SOLIDWORKS PART (.sldprt)
format: sldprt  version: not decoded by parser v0  size: 262,656 bytes
history: native  units: mm
features: sketch x7, cut_extrude x4, material x1, extrude x1, plane x1, mirror x1 (+13 scaffold rows collapsed)
feature tree (28):
  scaffold x13  (default folders/planes/origin — collapsed)
  material  "Material <not specified>"
  sketch  "Sketch1"  dims[D1=0.0mm]
  extrude  "Boss-Extrude1"  Depth=3mm
  sketch  "Sketch5"  dims[D1=~31.054982mm]
  plane  "Plane1"
  sketch  "Sketch2"
  sketch  "Sketch3"  dims[D1=0.0mm D2=0.0mm D3=0.0mm D4=0.0mm D5=0.0mm D6=0.0mm D7=0.0mm D8=0.0mm]
  cut_extrude  "Cut-Extrude1"  [1 undecoded]
  sketch  "Sketch4"  dims[D1=3.0mm D2=9.0mm D4=9.0mm D3=4.0]
  cut_extrude  "Cut-Extrude2"  [1 undecoded]
  mirror  "Mirror1"
  sketch  "Sketch6"  dims[D1=6.0mm]
  cut_extrude  "Cut-Extrude3"  [1 undecoded]
  sketch  "Sketch7"
  cut_extrude  "Cut-Extrude4"  [1 undecoded]
decode coverage: 6 of 13 modeling features carry decoded parameters
note: ~ marks probable driven/reference dimensions
note: 4 parameter values undecoded
summary: no parameter record found for 4 features
note: suppression state not decoded; provenance and decode notes live in map.json
